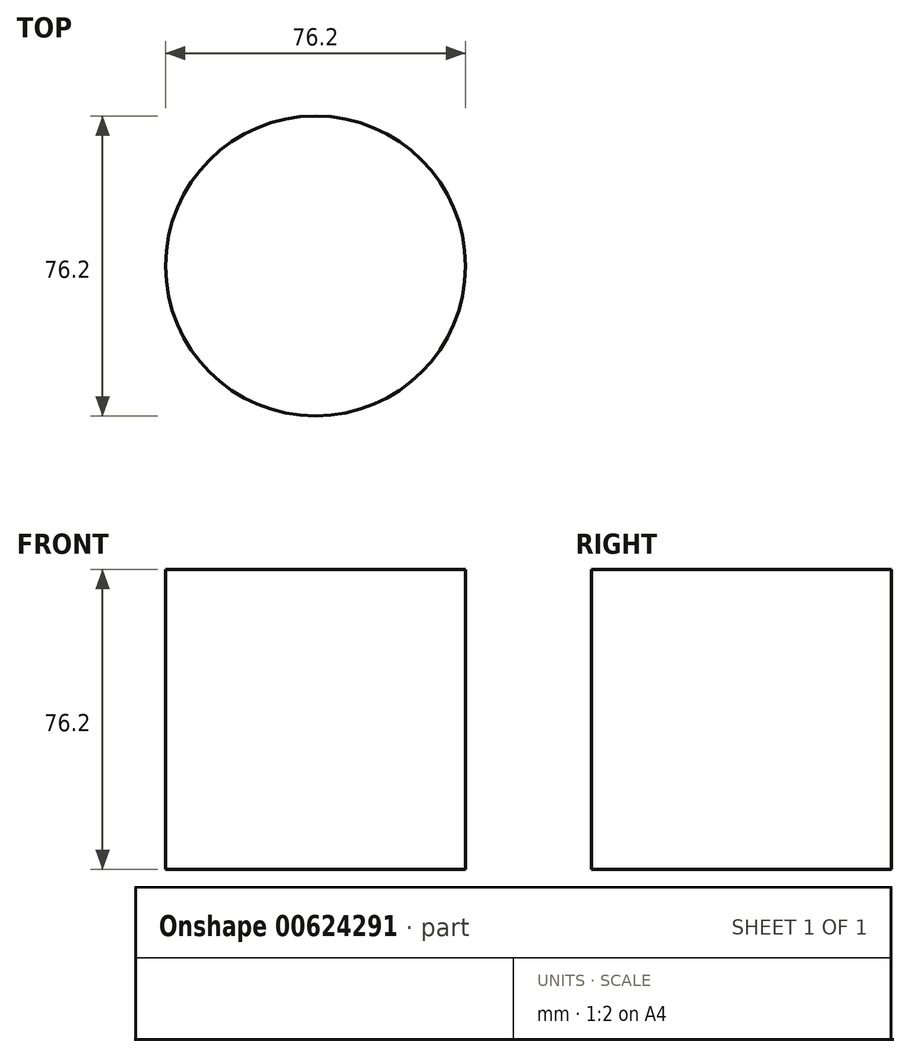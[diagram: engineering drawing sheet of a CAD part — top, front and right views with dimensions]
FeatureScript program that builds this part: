
annotation { "Feature Type Name" : "Feature", "Feature Type Description" : "" }
export const myFeature = defineFeature(function(context is Context, id is Id, definition is map)
    precondition{}
    {
        {
            var Q0;
            Q0=qCreatedBy(makeId("Top.planeOp"),FACE);
            var sketch = newSketch(context, id + "F0", { "sketchPlane" : qUnion([Q0])});
            skCircle(sketch, "E0", {"center": v(0, 0) * mm, "radius": 38.1 * mm});
            skSolve(sketch);
        }
        {
            var Q0;
            Q0=makeQuery(id+"F0.imprint","IMPRINT",FACE,{"disambiguationData":[TD([[makeQuery(id+"F0.imprint","IMPRINT",EDGE,{"derivedFrom":sQuery(id+"F0.wireOp",EDGE,"E0")}),1.0]])]});
            extrude(context, id + "F1", {"entities" : qUnion([Q0]), "depth" : 76.2 * mm, "offsetDistance" : 25.4 * mm});
        }
    });
